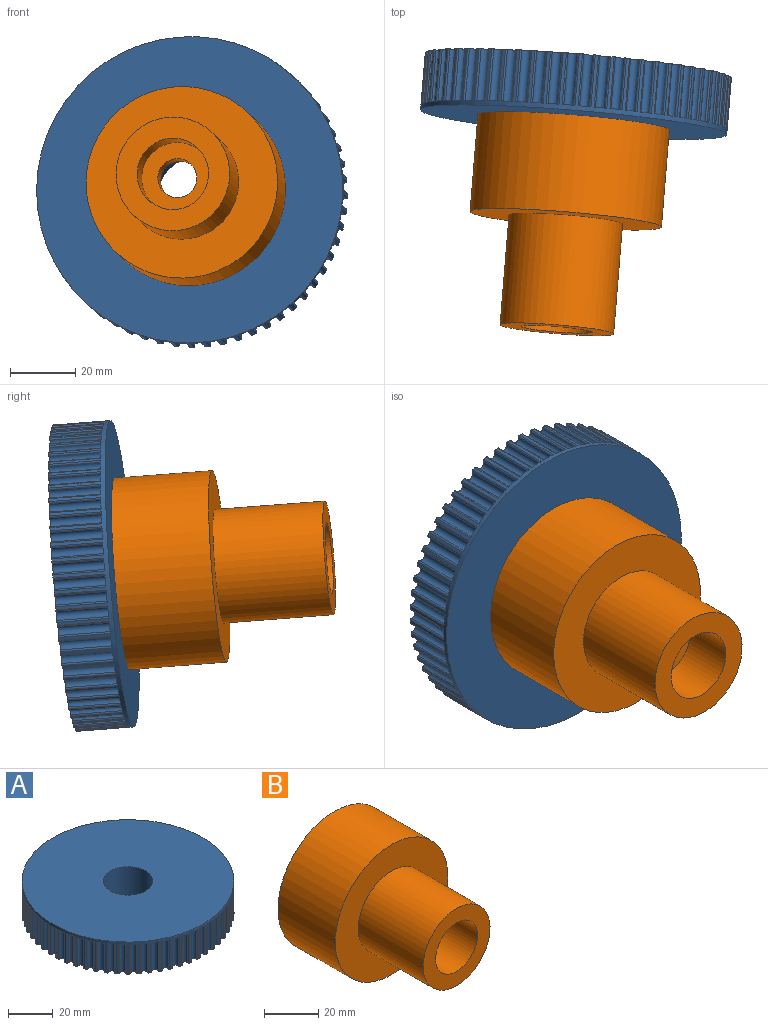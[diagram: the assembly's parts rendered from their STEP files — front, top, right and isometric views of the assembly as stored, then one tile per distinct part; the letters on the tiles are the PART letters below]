
ASSEMBLY  parts=2 mates=1
PART A: 244 faces, bbox 94.3x94.3x17.5 mm
  f0: cylinder r=0.45mm len=16mm, axis (0,0,1), area 11.9mm2, adj f2,f177,f178,f182
  f1: cylinder r=0.45mm len=16mm, axis (0,0,1), area 11.9mm2, adj f2,f177,f178,f182
  f2: cylinder r=1.5mm len=16mm, axis (0,0,1), area 77.1mm2, adj f0,f1,f178,f182
  f3: cylinder r=0.45mm len=16mm, axis (0,0,1), area 11.9mm2, adj f5,f177,f178,f183
  f4: cylinder r=0.45mm len=16mm, axis (0,0,1), area 11.9mm2, adj f5,f177,f178,f183
  f5: cylinder r=1.5mm len=16mm, axis (0,0,1), area 77.1mm2, adj f3,f4,f178,f183
  f6: cylinder r=0.45mm len=16mm, axis (0,0,1), area 11.9mm2, adj f8,f177,f178,f184
  f7: cylinder r=0.45mm len=16mm, axis (0,0,1), area 11.9mm2, adj f8,f177,f178,f184
  f8: cylinder r=1.5mm len=16mm, axis (0,0,1), area 77.1mm2, adj f6,f7,f178,f184
  f9: cylinder r=0.45mm len=16mm, axis (0,0,1), area 11.9mm2, adj f11,f177,f178,f185
  f10: cylinder r=0.45mm len=16mm, axis (0,0,1), area 11.9mm2, adj f11,f177,f178,f185
  f11: cylinder r=1.5mm len=16mm, axis (0,0,1), area 77.1mm2, adj f9,f10,f178,f185
  f12: cylinder r=0.45mm len=16mm, axis (0,0,1), area 11.9mm2, adj f14,f177,f178,f186
  f13: cylinder r=0.45mm len=16mm, axis (0,0,1), area 11.9mm2, adj f14,f177,f178,f186
  f14: cylinder r=1.5mm len=16mm, axis (0,0,1), area 77.1mm2, adj f12,f13,f178,f186
  f15: cylinder r=0.45mm len=16mm, axis (0,0,1), area 11.9mm2, adj f17,f177,f178,f187
  f16: cylinder r=0.45mm len=16mm, axis (0,0,1), area 11.9mm2, adj f17,f177,f178,f187
  f17: cylinder r=1.5mm len=16mm, axis (0,0,1), area 77.1mm2, adj f15,f16,f178,f187
  f18: cylinder r=0.45mm len=16mm, axis (0,0,1), area 11.9mm2, adj f20,f177,f178,f188
  f19: cylinder r=0.45mm len=16mm, axis (0,0,1), area 11.9mm2, adj f20,f177,f178,f188
  f20: cylinder r=1.5mm len=16mm, axis (0,0,1), area 77.1mm2, adj f18,f19,f178,f188
  f21: cylinder r=0.45mm len=16mm, axis (0,0,1), area 11.9mm2, adj f23,f177,f178,f189
  f22: cylinder r=0.45mm len=16mm, axis (0,0,1), area 11.9mm2, adj f23,f177,f178,f189
  f23: cylinder r=1.5mm len=16mm, axis (0,0,1), area 77.1mm2, adj f21,f22,f178,f189
  f24: cylinder r=0.45mm len=16mm, axis (0,0,1), area 11.9mm2, adj f26,f177,f178,f190
  f25: cylinder r=0.45mm len=16mm, axis (0,0,1), area 11.9mm2, adj f26,f177,f178,f190
  f26: cylinder r=1.5mm len=16mm, axis (0,0,1), area 77.1mm2, adj f24,f25,f178,f190
  f27: cylinder r=0.45mm len=16mm, axis (0,0,1), area 11.9mm2, adj f29,f177,f178,f191
  f28: cylinder r=0.45mm len=16mm, axis (0,0,1), area 11.9mm2, adj f29,f177,f178,f191
  f29: cylinder r=1.5mm len=16mm, axis (0,0,1), area 77.1mm2, adj f27,f28,f178,f191
  f30: cylinder r=0.45mm len=16mm, axis (0,0,1), area 11.9mm2, adj f32,f177,f178,f192
  f31: cylinder r=0.45mm len=16mm, axis (0,0,1), area 11.9mm2, adj f32,f177,f178,f192
  f32: cylinder r=1.5mm len=16mm, axis (0,0,1), area 77.1mm2, adj f30,f31,f178,f192
  f33: cylinder r=0.45mm len=16mm, axis (0,0,1), area 11.9mm2, adj f35,f177,f178,f193
  f34: cylinder r=0.45mm len=16mm, axis (0,0,1), area 11.9mm2, adj f35,f177,f178,f193
  f35: cylinder r=1.5mm len=16mm, axis (0,0,1), area 77.1mm2, adj f33,f34,f178,f193
  f36: cylinder r=0.45mm len=16mm, axis (0,0,1), area 11.9mm2, adj f38,f177,f178,f194
  f37: cylinder r=0.45mm len=16mm, axis (0,0,1), area 11.9mm2, adj f38,f177,f178,f194
  f38: cylinder r=1.5mm len=16mm, axis (0,0,1), area 77.1mm2, adj f36,f37,f178,f194
  f39: cylinder r=0.45mm len=16mm, axis (0,0,1), area 11.9mm2, adj f41,f177,f178,f195
  f40: cylinder r=0.45mm len=16mm, axis (0,0,1), area 11.9mm2, adj f41,f177,f178,f195
  f41: cylinder r=1.5mm len=16mm, axis (0,0,1), area 77.1mm2, adj f39,f40,f178,f195
  f42: cylinder r=0.45mm len=16mm, axis (0,0,1), area 11.9mm2, adj f44,f177,f178,f196
  f43: cylinder r=0.45mm len=16mm, axis (0,0,1), area 11.9mm2, adj f44,f177,f178,f196
  f44: cylinder r=1.5mm len=16mm, axis (0,0,1), area 77.1mm2, adj f42,f43,f178,f196
  f45: cylinder r=0.45mm len=16mm, axis (0,0,1), area 11.9mm2, adj f47,f177,f178,f197
  f46: cylinder r=0.45mm len=16mm, axis (0,0,1), area 11.9mm2, adj f47,f177,f178,f197
  f47: cylinder r=1.5mm len=16mm, axis (0,0,1), area 77.1mm2, adj f45,f46,f178,f197
  f48: cylinder r=0.45mm len=16mm, axis (0,0,1), area 11.9mm2, adj f50,f177,f178,f198
  f49: cylinder r=0.45mm len=16mm, axis (0,0,1), area 11.9mm2, adj f50,f177,f178,f198
  f50: cylinder r=1.5mm len=16mm, axis (0,0,1), area 77.1mm2, adj f48,f49,f178,f198
  f51: cylinder r=0.45mm len=16mm, axis (0,0,1), area 11.9mm2, adj f53,f177,f178,f199
  f52: cylinder r=0.45mm len=16mm, axis (0,0,1), area 11.9mm2, adj f53,f177,f178,f199
  f53: cylinder r=1.5mm len=16mm, axis (0,0,1), area 77.1mm2, adj f51,f52,f178,f199
  f54: cylinder r=0.45mm len=16mm, axis (0,0,1), area 11.9mm2, adj f56,f177,f178,f200
  f55: cylinder r=0.45mm len=16mm, axis (0,0,1), area 11.9mm2, adj f56,f177,f178,f200
  f56: cylinder r=1.5mm len=16mm, axis (0,0,1), area 77.1mm2, adj f54,f55,f178,f200
  f57: cylinder r=0.45mm len=16mm, axis (0,0,1), area 11.9mm2, adj f59,f177,f178,f201
  f58: cylinder r=0.45mm len=16mm, axis (0,0,1), area 11.9mm2, adj f59,f177,f178,f201
  f59: cylinder r=1.5mm len=16mm, axis (0,0,1), area 77.1mm2, adj f57,f58,f178,f201
  f60: cylinder r=0.45mm len=16mm, axis (0,0,1), area 11.9mm2, adj f62,f177,f178,f202
  f61: cylinder r=0.45mm len=16mm, axis (0,0,1), area 11.9mm2, adj f62,f177,f178,f202
  f62: cylinder r=1.5mm len=16mm, axis (0,0,1), area 77.1mm2, adj f60,f61,f178,f202
  f63: cylinder r=0.45mm len=16mm, axis (0,0,1), area 11.9mm2, adj f65,f177,f178,f203
  f64: cylinder r=0.45mm len=16mm, axis (0,0,1), area 11.9mm2, adj f65,f177,f178,f203
  f65: cylinder r=1.5mm len=16mm, axis (0,0,1), area 77.1mm2, adj f63,f64,f178,f203
  f66: cylinder r=0.45mm len=16mm, axis (0,0,1), area 11.9mm2, adj f68,f177,f178,f204
  f67: cylinder r=0.45mm len=16mm, axis (0,0,1), area 11.9mm2, adj f68,f177,f178,f204
  f68: cylinder r=1.5mm len=16mm, axis (0,0,1), area 77.1mm2, adj f66,f67,f178,f204
  f69: cylinder r=0.45mm len=16mm, axis (0,0,1), area 11.9mm2, adj f71,f177,f178,f205
  f70: cylinder r=0.45mm len=16mm, axis (0,0,1), area 11.9mm2, adj f71,f177,f178,f205
  f71: cylinder r=1.5mm len=16mm, axis (0,0,1), area 77.1mm2, adj f69,f70,f178,f205
  f72: cylinder r=0.45mm len=16mm, axis (0,0,1), area 11.9mm2, adj f74,f177,f178,f206
  f73: cylinder r=0.45mm len=16mm, axis (0,0,1), area 11.9mm2, adj f74,f177,f178,f206
  f74: cylinder r=1.5mm len=16mm, axis (0,0,1), area 77.1mm2, adj f72,f73,f178,f206
  f75: cylinder r=0.45mm len=16mm, axis (0,0,1), area 11.9mm2, adj f77,f177,f178,f207
  f76: cylinder r=0.45mm len=16mm, axis (0,0,1), area 11.9mm2, adj f77,f177,f178,f207
  f77: cylinder r=1.5mm len=16mm, axis (0,0,1), area 77.1mm2, adj f75,f76,f178,f207
  f78: cylinder r=0.45mm len=16mm, axis (0,0,1), area 11.9mm2, adj f80,f177,f178,f208
  f79: cylinder r=0.45mm len=16mm, axis (0,0,1), area 11.9mm2, adj f80,f177,f178,f208
  f80: cylinder r=1.5mm len=16mm, axis (0,0,1), area 77.1mm2, adj f78,f79,f178,f208
  f81: cylinder r=0.45mm len=16mm, axis (0,0,1), area 11.9mm2, adj f83,f177,f178,f209
  f82: cylinder r=0.45mm len=16mm, axis (0,0,1), area 11.9mm2, adj f83,f177,f178,f209
  f83: cylinder r=1.5mm len=16mm, axis (0,0,1), area 77.1mm2, adj f81,f82,f178,f209
  f84: cylinder r=0.45mm len=16mm, axis (0,0,1), area 11.9mm2, adj f86,f177,f178,f210
  f85: cylinder r=0.45mm len=16mm, axis (0,0,1), area 11.9mm2, adj f86,f177,f178,f210
  f86: cylinder r=1.5mm len=16mm, axis (0,0,1), area 77.1mm2, adj f84,f85,f178,f210
  f87: cylinder r=0.45mm len=16mm, axis (0,0,1), area 11.9mm2, adj f89,f177,f178,f211
  f88: cylinder r=0.45mm len=16mm, axis (0,0,1), area 11.9mm2, adj f89,f177,f178,f211
  f89: cylinder r=1.5mm len=16mm, axis (0,0,1), area 77.1mm2, adj f87,f88,f178,f211
  f90: cylinder r=0.45mm len=16mm, axis (0,0,1), area 11.9mm2, adj f92,f177,f178,f212
  f91: cylinder r=0.45mm len=16mm, axis (0,0,1), area 11.9mm2, adj f92,f177,f178,f212
  f92: cylinder r=1.5mm len=16mm, axis (0,0,1), area 77.1mm2, adj f90,f91,f178,f212
  f93: cylinder r=0.45mm len=16mm, axis (0,0,1), area 11.9mm2, adj f95,f177,f178,f213
  f94: cylinder r=0.45mm len=16mm, axis (0,0,1), area 11.9mm2, adj f95,f177,f178,f213
  f95: cylinder r=1.5mm len=16mm, axis (0,0,1), area 77.1mm2, adj f93,f94,f178,f213
  f96: cylinder r=0.45mm len=16mm, axis (0,0,1), area 11.9mm2, adj f98,f177,f178,f214
  f97: cylinder r=0.45mm len=16mm, axis (0,0,1), area 11.9mm2, adj f98,f177,f178,f214
  f98: cylinder r=1.5mm len=16mm, axis (0,0,1), area 77.1mm2, adj f96,f97,f178,f214
  f99: cylinder r=0.45mm len=16mm, axis (0,0,1), area 11.9mm2, adj f101,f177,f178,f215
  f100: cylinder r=0.45mm len=16mm, axis (0,0,1), area 11.9mm2, adj f101,f177,f178,f215
  f101: cylinder r=1.5mm len=16mm, axis (0,0,1), area 77.1mm2, adj f99,f100,f178,f215
  f102: cylinder r=0.45mm len=16mm, axis (0,0,1), area 11.9mm2, adj f104,f177,f178,f216
  f103: cylinder r=0.45mm len=16mm, axis (0,0,1), area 11.9mm2, adj f104,f177,f178,f216
  f104: cylinder r=1.5mm len=16mm, axis (0,0,1), area 77.1mm2, adj f102,f103,f178,f216
  f105: cylinder r=0.45mm len=16mm, axis (0,0,1), area 11.9mm2, adj f107,f177,f178,f217
  f106: cylinder r=0.45mm len=16mm, axis (0,0,1), area 11.9mm2, adj f107,f177,f178,f217
  f107: cylinder r=1.5mm len=16mm, axis (0,0,1), area 77.1mm2, adj f105,f106,f178,f217
  f108: cylinder r=0.45mm len=16mm, axis (0,0,1), area 11.9mm2, adj f110,f177,f178,f218
  f109: cylinder r=0.45mm len=16mm, axis (0,0,1), area 11.9mm2, adj f110,f177,f178,f218
  f110: cylinder r=1.5mm len=16mm, axis (0,0,1), area 77.1mm2, adj f108,f109,f178,f218
  f111: cylinder r=0.45mm len=16mm, axis (0,0,1), area 11.9mm2, adj f113,f177,f178,f219
  f112: cylinder r=0.45mm len=16mm, axis (0,0,1), area 11.9mm2, adj f113,f177,f178,f219
  f113: cylinder r=1.5mm len=16mm, axis (0,0,1), area 77.1mm2, adj f111,f112,f178,f219
  f114: cylinder r=0.45mm len=16mm, axis (0,0,1), area 11.9mm2, adj f116,f177,f178,f220
  f115: cylinder r=0.45mm len=16mm, axis (0,0,1), area 11.9mm2, adj f116,f177,f178,f220
  f116: cylinder r=1.5mm len=16mm, axis (0,0,1), area 77.1mm2, adj f114,f115,f178,f220
  f117: cylinder r=0.45mm len=16mm, axis (0,0,1), area 11.9mm2, adj f119,f177,f178,f221
  f118: cylinder r=0.45mm len=16mm, axis (0,0,1), area 11.9mm2, adj f119,f177,f178,f221
  f119: cylinder r=1.5mm len=16mm, axis (0,0,1), area 77.1mm2, adj f117,f118,f178,f221
  f120: cylinder r=0.45mm len=16mm, axis (0,0,1), area 11.9mm2, adj f122,f177,f178,f222
  f121: cylinder r=0.45mm len=16mm, axis (0,0,1), area 11.9mm2, adj f122,f177,f178,f222
  f122: cylinder r=1.5mm len=16mm, axis (0,0,1), area 77.1mm2, adj f120,f121,f178,f222
  f123: cylinder r=0.45mm len=16mm, axis (0,0,1), area 11.9mm2, adj f125,f177,f178,f223
  f124: cylinder r=0.45mm len=16mm, axis (0,0,1), area 11.9mm2, adj f125,f177,f178,f223
  f125: cylinder r=1.5mm len=16mm, axis (0,0,1), area 77.1mm2, adj f123,f124,f178,f223
  f126: cylinder r=0.45mm len=16mm, axis (0,0,1), area 11.9mm2, adj f128,f177,f178,f224
  f127: cylinder r=0.45mm len=16mm, axis (0,0,1), area 11.9mm2, adj f128,f177,f178,f224
  f128: cylinder r=1.5mm len=16mm, axis (0,0,1), area 77.1mm2, adj f126,f127,f178,f224
  f129: cylinder r=0.45mm len=16mm, axis (0,0,1), area 11.9mm2, adj f131,f177,f178,f225
  f130: cylinder r=0.45mm len=16mm, axis (0,0,1), area 11.9mm2, adj f131,f177,f178,f225
  f131: cylinder r=1.5mm len=16mm, axis (0,0,1), area 77.1mm2, adj f129,f130,f178,f225
  f132: cylinder r=0.45mm len=16mm, axis (0,0,1), area 11.9mm2, adj f134,f177,f178,f226
  f133: cylinder r=0.45mm len=16mm, axis (0,0,1), area 11.9mm2, adj f134,f177,f178,f226
  f134: cylinder r=1.5mm len=16mm, axis (0,0,1), area 77.1mm2, adj f132,f133,f178,f226
  f135: cylinder r=0.45mm len=16mm, axis (0,0,1), area 11.9mm2, adj f137,f177,f178,f227
  f136: cylinder r=0.45mm len=16mm, axis (0,0,1), area 11.9mm2, adj f137,f177,f178,f227
  f137: cylinder r=1.5mm len=16mm, axis (0,0,1), area 77.1mm2, adj f135,f136,f178,f227
  f138: cylinder r=0.45mm len=16mm, axis (0,0,1), area 11.9mm2, adj f140,f177,f178,f228
  f139: cylinder r=0.45mm len=16mm, axis (0,0,1), area 11.9mm2, adj f140,f177,f178,f228
  f140: cylinder r=1.5mm len=16mm, axis (0,0,1), area 77.1mm2, adj f138,f139,f178,f228
  f141: cylinder r=0.45mm len=16mm, axis (0,0,1), area 11.9mm2, adj f143,f177,f178,f229
  f142: cylinder r=0.45mm len=16mm, axis (0,0,1), area 11.9mm2, adj f143,f177,f178,f229
  f143: cylinder r=1.5mm len=16mm, axis (0,0,1), area 77.1mm2, adj f141,f142,f178,f229
  f144: cylinder r=0.45mm len=16mm, axis (0,0,1), area 11.9mm2, adj f146,f177,f178,f230
  f145: cylinder r=0.45mm len=16mm, axis (0,0,1), area 11.9mm2, adj f146,f177,f178,f230
  f146: cylinder r=1.5mm len=16mm, axis (0,0,1), area 77.1mm2, adj f144,f145,f178,f230
  f147: cylinder r=0.45mm len=16mm, axis (0,0,1), area 11.9mm2, adj f149,f177,f178,f231
  f148: cylinder r=0.45mm len=16mm, axis (0,0,1), area 11.9mm2, adj f149,f177,f178,f231
  f149: cylinder r=1.5mm len=16mm, axis (0,0,1), area 77.1mm2, adj f147,f148,f178,f231
  f150: cylinder r=0.45mm len=16mm, axis (0,0,1), area 11.9mm2, adj f152,f177,f178,f232
  f151: cylinder r=0.45mm len=16mm, axis (0,0,1), area 11.9mm2, adj f152,f177,f178,f232
  f152: cylinder r=1.5mm len=16mm, axis (0,0,1), area 77.1mm2, adj f150,f151,f178,f232
  f153: cylinder r=0.45mm len=16mm, axis (0,0,1), area 11.9mm2, adj f155,f177,f178,f233
  f154: cylinder r=0.45mm len=16mm, axis (0,0,1), area 11.9mm2, adj f155,f177,f178,f233
  f155: cylinder r=1.5mm len=16mm, axis (0,0,1), area 77.1mm2, adj f153,f154,f178,f233
  f156: cylinder r=0.45mm len=16mm, axis (0,0,1), area 11.9mm2, adj f158,f177,f178,f234
  f157: cylinder r=0.45mm len=16mm, axis (0,0,1), area 11.9mm2, adj f158,f177,f178,f234
  f158: cylinder r=1.5mm len=16mm, axis (0,0,1), area 77.1mm2, adj f156,f157,f178,f234
  f159: cylinder r=0.45mm len=16mm, axis (0,0,1), area 11.9mm2, adj f161,f177,f178,f235
  f160: cylinder r=0.45mm len=16mm, axis (0,0,1), area 11.9mm2, adj f161,f177,f178,f235
  f161: cylinder r=1.5mm len=16mm, axis (0,0,1), area 77.1mm2, adj f159,f160,f178,f235
  f162: cylinder r=0.45mm len=16mm, axis (0,0,1), area 11.9mm2, adj f164,f177,f178,f236
  f163: cylinder r=0.45mm len=16mm, axis (0,0,1), area 11.9mm2, adj f164,f177,f178,f236
  f164: cylinder r=1.5mm len=16mm, axis (0,0,1), area 77.1mm2, adj f162,f163,f178,f236
  f165: cylinder r=0.45mm len=16mm, axis (0,0,1), area 11.9mm2, adj f167,f177,f178,f237
  f166: cylinder r=0.45mm len=16mm, axis (0,0,1), area 11.9mm2, adj f167,f177,f178,f237
  f167: cylinder r=1.5mm len=16mm, axis (0,0,1), area 77.1mm2, adj f165,f166,f178,f237
  f168: cylinder r=0.45mm len=16mm, axis (0,0,1), area 11.9mm2, adj f170,f177,f178,f238
  f169: cylinder r=0.45mm len=16mm, axis (0,0,1), area 11.9mm2, adj f170,f177,f178,f238
  f170: cylinder r=1.5mm len=16mm, axis (0,0,1), area 77.1mm2, adj f168,f169,f178,f238
  f171: cylinder r=0.45mm len=16mm, axis (0,0,1), area 11.9mm2, adj f173,f177,f178,f239
  f172: cylinder r=0.45mm len=16mm, axis (0,0,1), area 11.9mm2, adj f173,f177,f178,f239
  f173: cylinder r=1.5mm len=16mm, axis (0,0,1), area 77.1mm2, adj f171,f172,f178,f239
  f174: cylinder r=0.45mm len=16mm, axis (0,0,1), area 11.9mm2, adj f176,f177,f178,f240
  f175: cylinder r=0.45mm len=16mm, axis (0,0,1), area 11.9mm2, adj f176,f177,f178,f240
  f176: cylinder r=1.5mm len=16mm, axis (0,0,1), area 77.1mm2, adj f174,f175,f178,f240
  f177: cylinder r=47.17mm len=94.35mm, axis (0,0,-1), area 1408.3mm2, adj f0,f1,f3,f4,f6,f7,f9,f10
  f178: plane 94.27x94.27mm, normal (0,0,-1), area 6294.1mm2, adj f0,f1,f2,f3,f4,f5,f6,f7
  f179: cylinder r=0.45mm len=16mm, axis (0,0,1), area 11.9mm2, adj f177,f178,f181,f242
  f180: cylinder r=0.45mm len=16mm, axis (0,0,1), area 11.9mm2, adj f177,f178,f181,f242
  f181: cylinder r=1.5mm len=16mm, axis (0,0,1), area 77.1mm2, adj f178,f179,f180,f242
  f182: plane 3.91x2.22mm, normal (0,0,-1), area 5.3mm2, adj f0,f1,f2,f177
  f183: plane 3.85x2.42mm, normal (0,0,-1), area 5.3mm2, adj f3,f4,f5,f177
  f184: plane 3.74x2.6mm, normal (0,0,-1), area 5.3mm2, adj f6,f7,f8,f177
  f185: plane 3.6x2.77mm, normal (0,0,-1), area 5.3mm2, adj f9,f10,f11,f177
  f186: plane 3.46x2.93mm, normal (0,0,-1), area 5.3mm2, adj f12,f13,f14,f177
  f187: plane 3.4x3.08mm, normal (0,0,-1), area 5.3mm2, adj f15,f16,f17,f177
  f188: plane 3.31x3.2mm, normal (0,0,-1), area 5.3mm2, adj f18,f19,f20,f177
  f189: plane 3.31x3.2mm, normal (0,0,-1), area 5.3mm2, adj f21,f22,f23,f177
  f190: plane 3.4x3.08mm, normal (0,0,-1), area 5.3mm2, adj f24,f25,f26,f177
  f191: plane 3.46x2.93mm, normal (0,0,-1), area 5.3mm2, adj f27,f28,f29,f177
  f192: plane 3.6x2.77mm, normal (0,0,-1), area 5.3mm2, adj f30,f31,f32,f177
  f193: plane 3.74x2.6mm, normal (0,0,-1), area 5.3mm2, adj f33,f34,f35,f177
  f194: plane 3.85x2.42mm, normal (0,0,-1), area 5.3mm2, adj f36,f37,f38,f177
  f195: plane 3.91x2.22mm, normal (0,0,-1), area 5.3mm2, adj f39,f40,f41,f177
  f196: plane 3.94x2.06mm, normal (0,0,-1), area 5.3mm2, adj f42,f43,f44,f177
  f197: plane 3.91x2.22mm, normal (0,0,-1), area 5.3mm2, adj f45,f46,f47,f177
  f198: plane 3.85x2.42mm, normal (0,0,-1), area 5.3mm2, adj f48,f49,f50,f177
  f199: plane 3.74x2.6mm, normal (0,0,-1), area 5.3mm2, adj f51,f52,f53,f177
  f200: plane 3.6x2.77mm, normal (0,0,-1), area 5.3mm2, adj f54,f55,f56,f177
  f201: plane 3.46x2.93mm, normal (0,0,-1), area 5.3mm2, adj f57,f58,f59,f177
  f202: plane 3.4x3.08mm, normal (0,0,-1), area 5.3mm2, adj f60,f61,f62,f177
  f203: plane 3.31x3.2mm, normal (0,0,-1), area 5.3mm2, adj f63,f64,f65,f177
  f204: plane 3.31x3.2mm, normal (0,0,-1), area 5.3mm2, adj f66,f67,f68,f177
  f205: plane 3.4x3.08mm, normal (0,0,-1), area 5.3mm2, adj f69,f70,f71,f177
  f206: plane 3.46x2.93mm, normal (0,0,-1), area 5.3mm2, adj f72,f73,f74,f177
  f207: plane 3.6x2.77mm, normal (0,0,-1), area 5.3mm2, adj f75,f76,f77,f177
  f208: plane 3.74x2.6mm, normal (0,0,-1), area 5.3mm2, adj f78,f79,f80,f177
  f209: plane 3.85x2.42mm, normal (0,0,-1), area 5.3mm2, adj f81,f82,f83,f177
  f210: plane 3.91x2.22mm, normal (0,0,-1), area 5.3mm2, adj f84,f85,f86,f177
  f211: plane 3.94x2.06mm, normal (0,0,-1), area 5.3mm2, adj f87,f88,f89,f177
  f212: plane 3.91x2.22mm, normal (0,0,-1), area 5.3mm2, adj f90,f91,f92,f177
  f213: plane 3.85x2.42mm, normal (0,0,-1), area 5.3mm2, adj f93,f94,f95,f177
  f214: plane 3.74x2.6mm, normal (0,0,-1), area 5.3mm2, adj f96,f97,f98,f177
  f215: plane 3.6x2.77mm, normal (0,0,-1), area 5.3mm2, adj f99,f100,f101,f177
  f216: plane 3.46x2.93mm, normal (0,0,-1), area 5.3mm2, adj f102,f103,f104,f177
  f217: plane 3.4x3.08mm, normal (0,0,-1), area 5.3mm2, adj f105,f106,f107,f177
  f218: plane 3.31x3.2mm, normal (0,0,-1), area 5.3mm2, adj f108,f109,f110,f177
  f219: plane 3.31x3.2mm, normal (0,0,-1), area 5.3mm2, adj f111,f112,f113,f177
  f220: plane 3.4x3.08mm, normal (0,0,-1), area 5.3mm2, adj f114,f115,f116,f177
  f221: plane 3.46x2.93mm, normal (0,0,-1), area 5.3mm2, adj f117,f118,f119,f177
  f222: plane 3.6x2.77mm, normal (0,0,-1), area 5.3mm2, adj f120,f121,f122,f177
  f223: plane 3.74x2.6mm, normal (0,0,-1), area 5.3mm2, adj f123,f124,f125,f177
  f224: plane 3.85x2.42mm, normal (0,0,-1), area 5.3mm2, adj f126,f127,f128,f177
  f225: plane 3.91x2.22mm, normal (0,0,-1), area 5.3mm2, adj f129,f130,f131,f177
  f226: plane 3.94x2.06mm, normal (0,0,-1), area 5.3mm2, adj f132,f133,f134,f177
  f227: plane 3.91x2.22mm, normal (0,0,-1), area 5.3mm2, adj f135,f136,f137,f177
  f228: plane 3.85x2.42mm, normal (0,0,-1), area 5.3mm2, adj f138,f139,f140,f177
  f229: plane 3.74x2.6mm, normal (0,0,-1), area 5.3mm2, adj f141,f142,f143,f177
  f230: plane 3.6x2.77mm, normal (0,0,-1), area 5.3mm2, adj f144,f145,f146,f177
  f231: plane 3.46x2.93mm, normal (0,0,-1), area 5.3mm2, adj f147,f148,f149,f177
  f232: plane 3.4x3.08mm, normal (0,0,-1), area 5.3mm2, adj f150,f151,f152,f177
  f233: plane 3.31x3.2mm, normal (0,0,-1), area 5.3mm2, adj f153,f154,f155,f177
  f234: plane 3.31x3.2mm, normal (0,0,-1), area 5.3mm2, adj f156,f157,f158,f177
  f235: plane 3.4x3.08mm, normal (0,0,-1), area 5.3mm2, adj f159,f160,f161,f177
  f236: plane 3.46x2.93mm, normal (0,0,-1), area 5.3mm2, adj f162,f163,f164,f177
  f237: plane 3.6x2.77mm, normal (0,0,-1), area 5.3mm2, adj f165,f166,f167,f177
  f238: plane 3.74x2.6mm, normal (0,0,-1), area 5.3mm2, adj f168,f169,f170,f177
  f239: plane 3.85x2.42mm, normal (0,0,-1), area 5.3mm2, adj f171,f172,f173,f177
  f240: plane 3.91x2.22mm, normal (0,0,-1), area 5.3mm2, adj f174,f175,f176,f177
  f241: plane 94.35x94.35mm, normal (0,0,1), area 6611.1mm2, adj f177,f243
  f242: plane 3.94x2.06mm, normal (0,0,-1), area 5.3mm2, adj f177,f179,f180,f181
  f243: cylinder r=11mm len=22mm, axis (0,0,-1), area 1209.5mm2, adj f178,f241
PART B: 10 faces, bbox 59x64x59 mm
  f0: plane 22x22mm, normal (0,1,0), area 267mm2, adj f2,f5
  f1: plane 22x22mm, normal (0,-1,0), area 267mm2, adj f2,f4
  f2: cylinder r=6mm len=12mm, axis (0,1,0), area 377mm2, adj f0,f1
  f3: cylinder r=17.5mm len=35mm, axis (0,1,0), area 3738.5mm2, adj f8,f9
  f4: cylinder r=11mm len=22mm, axis (0,1,0), area 1175mm2, adj f1,f9
  f5: cylinder r=11mm len=37mm, axis (0,-1,0), area 2557.3mm2, adj f0,f7
  f6: cylinder r=29.5mm len=59mm, axis (0,-1,0), area 5560.6mm2, adj f7,f8
  f7: plane 59x59mm, normal (0,1,0), area 2353.8mm2, adj f5,f6
  f8: plane 59x59mm, normal (0,-1,0), area 1771.9mm2, adj f3,f6
  f9: plane 35x35mm, normal (0,-1,0), area 582mm2, adj f3,f4
PLACE A rot(axis=(0.61,-0.56,0.55),109.3deg) t=(74.72,158.4,-20.63)mm
PLACE B rot(axis=(-0.34,0.84,-0.43),11.7deg) t=(69.92,99.27,-16.1)mm
MATE fastened B.f4 <-> A.f177  axis (-0.08,-0.99,0.08) through (73.31,141.01,-19.29)mm
